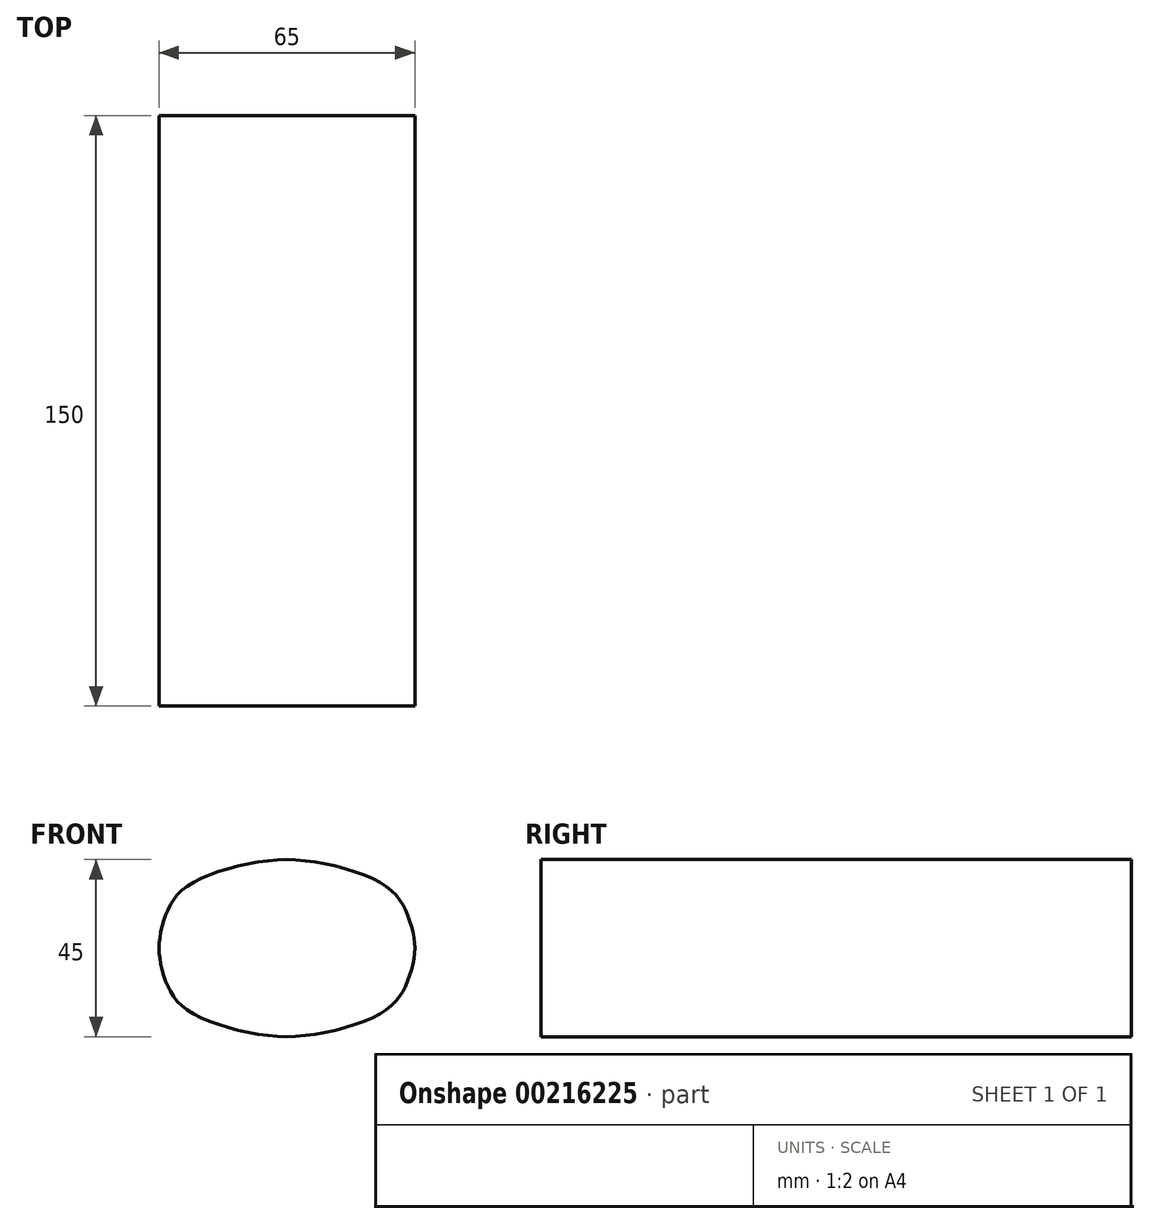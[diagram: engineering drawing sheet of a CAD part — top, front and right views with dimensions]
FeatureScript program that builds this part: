
annotation { "Feature Type Name" : "Feature", "Feature Type Description" : "" }
export const myFeature = defineFeature(function(context is Context, id is Id, definition is map)
    precondition{}
    {
        {
            var Q0;
            Q0=qCreatedBy(makeId("Front.planeOp"),FACE);
            var sketch = newSketch(context, id + "F0", { "sketchPlane" : qUnion([Q0])});
            skLineSegment(sketch, "E0", {"start": v(0, 40.3) * mm, "end": v(0, 0) * mm, "construction": true});
            skLineSegment(sketch, "E1", {"start": v(0, 0) * mm, "end": v(44.4, 0) * mm, "construction": true});
            skFitSpline(sketch, "E2", {"points": [v(0, 22.5) * mm, v(24.2, 16.39) * mm, v(30.7, 8.5) * mm, v(32.58, 0) * mm], "startDerivative": vector(50.82, 0) * mm, "endDerivative": vector(0, -28.17) * mm});
            skFitSpline(sketch, "E3.MirrorCS", {"points": [v(0, -22.5) * mm, v(24.2, -16.39) * mm, v(30.7, -8.5) * mm, v(32.58, 0) * mm], "startDerivative": vector(50.82, 0) * mm, "endDerivative": vector(0, 28.17) * mm});
            skFitSpline(sketch, "E4.MirrorCS", {"points": [v(0, -22.5) * mm, v(-24.2, -16.39) * mm, v(-30.7, -8.5) * mm, v(-32.42, 0) * mm], "startDerivative": vector(-50.88, 0) * mm, "endDerivative": vector(0, 28.19) * mm});
            skFitSpline(sketch, "E5.MirrorCS", {"points": [v(0, 22.5) * mm, v(-24.2, 16.39) * mm, v(-30.7, 8.5) * mm, v(-32.42, 0) * mm], "startDerivative": vector(-50.88, 0) * mm, "endDerivative": vector(0, -28.19) * mm});
            skSolve(sketch);
        }
        {
            var Q0;
            Q0 = qSketchRegion(id + "F0", true);
            extrude(context, id + "F1", {"entities" : qUnion([Q0]), "depth" : 150 * mm});
        }
    });
